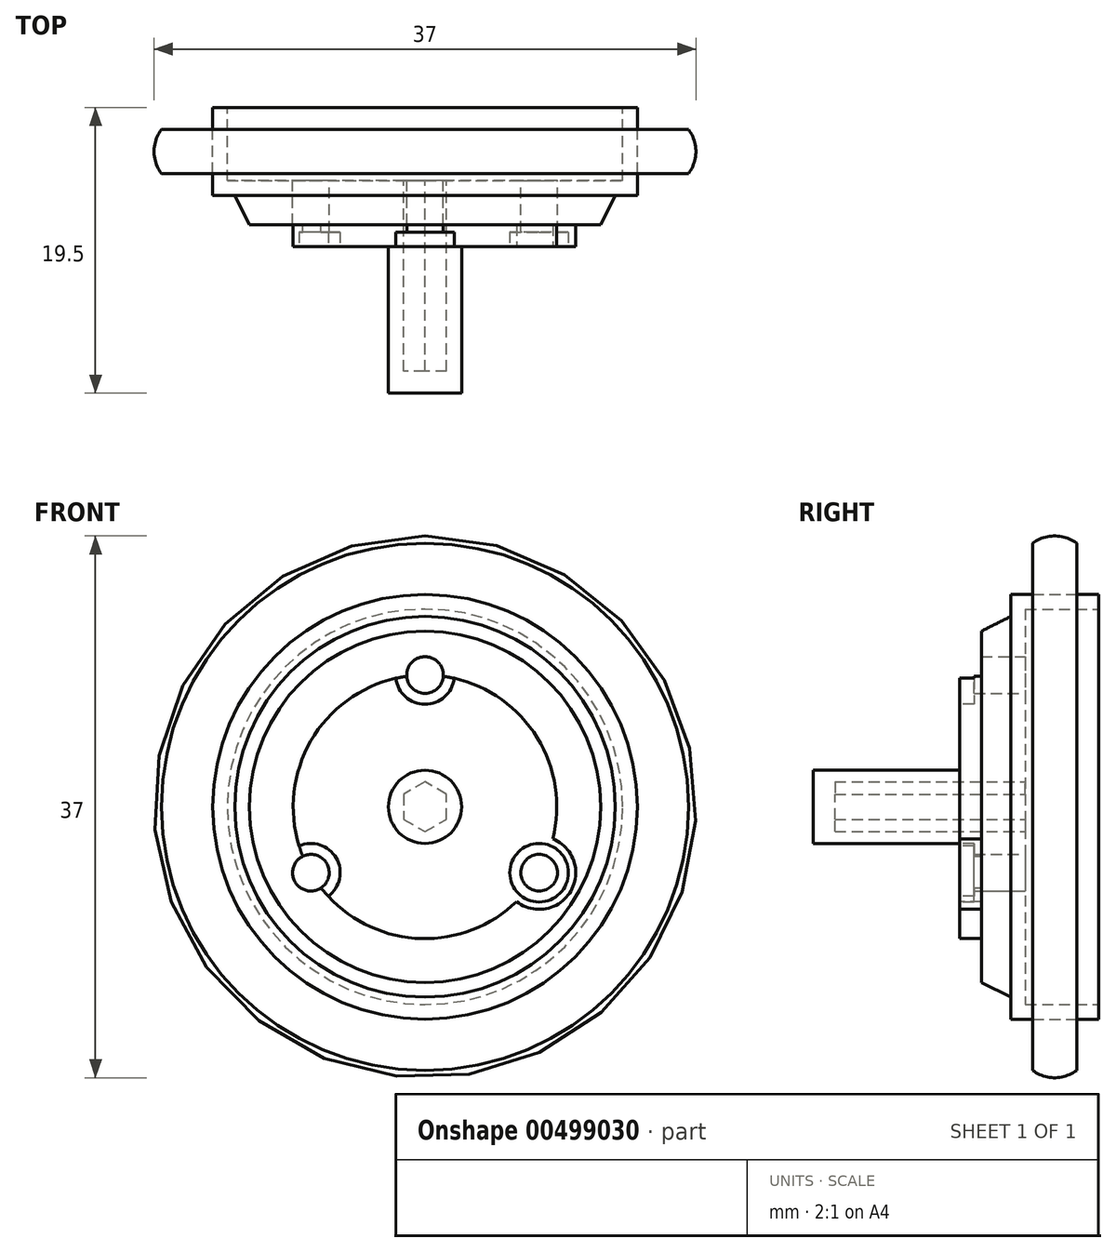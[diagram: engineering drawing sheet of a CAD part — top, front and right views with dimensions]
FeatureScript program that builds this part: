
annotation { "Feature Type Name" : "Feature", "Feature Type Description" : "" }
export const myFeature = defineFeature(function(context is Context, id is Id, definition is map)
    precondition{}
    {
        {
            var Q0;
            Q0=qCreatedBy(makeId("Front.planeOp"),FACE);
            var sketch = newSketch(context, id + "F0", { "sketchPlane" : qUnion([Q0])});
            skCircle(sketch, "E0", {"center": v(0, 0) * mm, "radius": 14.5 * mm});
            skSolve(sketch);
        }
        {
            var Q0;
            Q0=makeQuery(id+"F0.imprint","IMPRINT",FACE,{"disambiguationData":[TD([[makeQuery(id+"F0.imprint","IMPRINT",EDGE,{"derivedFrom":sQuery(id+"F0.wireOp",EDGE,"E0")}),1.0]])]});
            extrude(context, id + "F1", {"entities" : qUnion([Q0]), "depth" : 6 * mm});
        }
        {
            var Q0;
            Q0=qCreatedBy(makeId("Right.planeOp"),FACE);
            var sketch = newSketch(context, id + "F2", { "sketchPlane" : qUnion([Q0])});
            skLineSegment(sketch, "E1.0", {"start": v(-6, -14.5) * mm, "end": v(-6, 14.5) * mm, "construction": true});
            skLineSegment(sketch, "E2", {"start": v(-6, 0) * mm, "end": v(-8, 0) * mm});
            skPoint(sketch, "E2.endSnap0", {"position": v(-6, 0) * mm});
            skLineSegment(sketch, "E3", {"start": v(-8, 0) * mm, "end": v(-8, 12) * mm});
            skLineSegment(sketch, "E4", {"start": v(-8, 12) * mm, "end": v(-6, 13) * mm});
            skLineSegment(sketch, "E5", {"start": v(-6, 13) * mm, "end": v(-6, 0) * mm});
            skSolve(sketch);
        }
        {
            var Q0;
            Q0=makeQuery(id+"F2.imprint","IMPRINT",FACE,{"disambiguationData":[TD([[makeQuery(id+"F2.imprint","IMPRINT",EDGE,{"derivedFrom":sQuery(id+"F2.wireOp",EDGE,"E2")}),-1.0]])]});
            var Q1;
            Q1=sQuery(id+"F2.wireOp",EDGE,"E2");
            revolve(context, id + "F3", {"operationType" : NewBodyOperationType.ADD, "entities" : qUnion([Q0]), "axis" : qUnion([Q1]), "revolveType" : RevolveType.FULL});
        }
        {
            var Q0;
            Q0=makeQuery(id+"F3.opRevolve","SWEPT_FACE",FACE,{"disambiguationData":[OSD([sQuery(id+"F2.wireOp",EDGE,"E3")])]});
            var sketch = newSketch(context, id + "F4", { "sketchPlane" : qUnion([Q0])});
            skCircle(sketch, "E6", {"center": v(0, 0) * mm, "radius": 9 * mm});
            skSolve(sketch);
        }
        {
            var Q0;
            Q0=makeQuery(id+"F4.imprint","IMPRINT",FACE,{"disambiguationData":[TD([[makeQuery(id+"F4.imprint","IMPRINT",EDGE,{"derivedFrom":sQuery(id+"F4.wireOp",EDGE,"E6")}),1.0]])]});
            extrude(context, id + "F5", {"entities" : qUnion([Q0]), "operationType" : NewBodyOperationType.ADD, "depth" : 1.5 * mm});
        }
        {
            var Q0;
            Q0=makeQuery(id+"F5.opExtrude","CAP_FACE",FACE,{"disambiguationData":[OSD([sQuery(id+"F4.wireOp",EDGE,"E6")])],"isStart":false});
            var sketch = newSketch(context, id + "F6", { "sketchPlane" : qUnion([Q0])});
            skCircle(sketch, "E7", {"center": v(0, 0) * mm, "radius": 2.5 * mm});
            skSolve(sketch);
        }
        {
            var Q0;
            Q0=makeQuery(id+"F6.imprint","IMPRINT",FACE,{"disambiguationData":[TD([[makeQuery(id+"F6.imprint","IMPRINT",EDGE,{"derivedFrom":sQuery(id+"F6.wireOp",EDGE,"E7")}),1.0]])]});
            extrude(context, id + "F7", {"entities" : qUnion([Q0]), "operationType" : NewBodyOperationType.ADD, "depth" : 10 * mm});
        }
        {
            var Q0;
            Q0=makeQuery(id+"F5.opExtrude","CAP_FACE",FACE,{"disambiguationData":[OSD([sQuery(id+"F4.wireOp",EDGE,"E6")])],"isStart":false});
            var sketch = newSketch(context, id + "F8", { "sketchPlane" : qUnion([Q0])});
            skCircle(sketch, "E8.0", {"center": v(0, 0) * mm, "radius": 9 * mm, "construction": true});
            skLineSegment(sketch, "E9.0", {"start": v(0, 9) * mm, "end": v(7.8, -4.5) * mm});
            skLineSegment(sketch, "E9.1", {"start": v(7.8, -4.5) * mm, "end": v(-7.8, -4.5) * mm});
            skLineSegment(sketch, "E9.2", {"start": v(-7.8, -4.5) * mm, "end": v(0, 9) * mm});
            skCircle(sketch, "E10", {"center": v(0, 9) * mm, "radius": 2.5 * mm});
            skCircle(sketch, "E11", {"center": v(7.8, -4.5) * mm, "radius": 2.5 * mm});
            skCircle(sketch, "E12", {"center": v(-7.8, -4.5) * mm, "radius": 2.5 * mm});
            skSolve(sketch);
        }
        {
            var Q0;
            {var subQ0=sQuery(id+"F8.wireOp",EDGE,"E9.0");var subQ3=sQuery(id+"F8.wireOp",EDGE,"E11");var subQ4=makeQuery(id+"F8.imprint","INTERSECT",VERTEX,{"derivedFrom":[subQ0,subQ3]});Q0=makeQuery(id+"F8.imprint","IMPRINT",FACE,{"disambiguationData":[TD([[makeQuery(id+"F8.imprint","IMPRINT",EDGE,{"disambiguationData":[TD([[subQ4,1.0]])],"derivedFrom":subQ3}),1.0]])]});}
            var Q1;
            {var subQ0=sQuery(id+"F8.wireOp",EDGE,"E11");var subQ1=makeQuery(id+"F5.opExtrude","CAP_EDGE",EDGE,{"disambiguationData":[OSD([sQuery(id+"F4.wireOp",EDGE,"E6")])],"isStart":false});var subQ2=makeQuery(id+"F8.imprint","INTERSECT",VERTEX,{"disambiguationData":[OD(0.0)],"derivedFrom":[subQ1,subQ0]});Q1=makeQuery(id+"F8.imprint","IMPRINT",FACE,{"disambiguationData":[TD([[makeQuery(id+"F8.imprint","IMPRINT",EDGE,{"disambiguationData":[TD([[subQ2,1.0]])],"derivedFrom":subQ0}),1.0]])]});}
            var Q2;
            {var subQ0=sQuery(id+"F8.wireOp",EDGE,"E9.1");var subQ3=sQuery(id+"F8.wireOp",EDGE,"E11");var subQ4=makeQuery(id+"F8.imprint","INTERSECT",VERTEX,{"derivedFrom":[subQ0,subQ3]});Q2=makeQuery(id+"F8.imprint","IMPRINT",FACE,{"disambiguationData":[TD([[makeQuery(id+"F8.imprint","IMPRINT",EDGE,{"disambiguationData":[TD([[subQ4,-1.0]])],"derivedFrom":subQ3}),1.0]])]});}
            var Q3;
            {var subQ1=sQuery(id+"F8.wireOp",EDGE,"E9.0");var subQ3=sQuery(id+"F8.wireOp",EDGE,"E11");var subQ4=makeQuery(id+"F8.imprint","INTERSECT",VERTEX,{"derivedFrom":[subQ1,subQ3]});Q3=makeQuery(id+"F8.imprint","IMPRINT",FACE,{"disambiguationData":[TD([[makeQuery(id+"F8.imprint","IMPRINT",EDGE,{"disambiguationData":[TD([[subQ4,-1.0]])],"derivedFrom":subQ3}),1.0]])]});}
            var Q4;
            {var subQ1=sQuery(id+"F8.wireOp",EDGE,"E9.1");var subQ3=sQuery(id+"F8.wireOp",EDGE,"E12");var subQ4=makeQuery(id+"F8.imprint","INTERSECT",VERTEX,{"derivedFrom":[subQ1,subQ3]});Q4=makeQuery(id+"F8.imprint","IMPRINT",FACE,{"disambiguationData":[TD([[makeQuery(id+"F8.imprint","IMPRINT",EDGE,{"disambiguationData":[TD([[subQ4,-1.0]])],"derivedFrom":subQ3}),1.0]])]});}
            var Q5;
            {var subQ0=sQuery(id+"F8.wireOp",EDGE,"E9.2");var subQ3=sQuery(id+"F8.wireOp",EDGE,"E12");var subQ4=makeQuery(id+"F8.imprint","INTERSECT",VERTEX,{"derivedFrom":[subQ0,subQ3]});Q5=makeQuery(id+"F8.imprint","IMPRINT",FACE,{"disambiguationData":[TD([[makeQuery(id+"F8.imprint","IMPRINT",EDGE,{"disambiguationData":[TD([[subQ4,-1.0]])],"derivedFrom":subQ3}),1.0]])]});}
            var Q6;
            {var subQ0=sQuery(id+"F8.wireOp",EDGE,"E12");var subQ1=makeQuery(id+"F5.opExtrude","CAP_EDGE",EDGE,{"disambiguationData":[OSD([sQuery(id+"F4.wireOp",EDGE,"E6")])],"isStart":false});var subQ2=makeQuery(id+"F8.imprint","INTERSECT",VERTEX,{"disambiguationData":[OD(0.0)],"derivedFrom":[subQ1,subQ0]});Q6=makeQuery(id+"F8.imprint","IMPRINT",FACE,{"disambiguationData":[TD([[makeQuery(id+"F8.imprint","IMPRINT",EDGE,{"disambiguationData":[TD([[subQ2,-1.0]])],"derivedFrom":subQ0}),1.0]])]});}
            var Q7;
            {var subQ0=sQuery(id+"F8.wireOp",EDGE,"E9.1");var subQ3=sQuery(id+"F8.wireOp",EDGE,"E12");var subQ4=makeQuery(id+"F8.imprint","INTERSECT",VERTEX,{"derivedFrom":[subQ0,subQ3]});Q7=makeQuery(id+"F8.imprint","IMPRINT",FACE,{"disambiguationData":[TD([[makeQuery(id+"F8.imprint","IMPRINT",EDGE,{"disambiguationData":[TD([[subQ4,1.0]])],"derivedFrom":subQ3}),1.0]])]});}
            var Q8;
            {var subQ0=sQuery(id+"F8.wireOp",EDGE,"E9.2");var subQ3=sQuery(id+"F8.wireOp",EDGE,"E10");var subQ4=makeQuery(id+"F8.imprint","INTERSECT",VERTEX,{"derivedFrom":[subQ0,subQ3]});Q8=makeQuery(id+"F8.imprint","IMPRINT",FACE,{"disambiguationData":[TD([[makeQuery(id+"F8.imprint","IMPRINT",EDGE,{"disambiguationData":[TD([[subQ4,1.0]])],"derivedFrom":subQ3}),1.0]])]});}
            var Q9;
            {var subQ1=sQuery(id+"F8.wireOp",EDGE,"E9.0");var subQ3=sQuery(id+"F8.wireOp",EDGE,"E10");var subQ4=makeQuery(id+"F8.imprint","INTERSECT",VERTEX,{"derivedFrom":[subQ1,subQ3]});Q9=makeQuery(id+"F8.imprint","IMPRINT",FACE,{"disambiguationData":[TD([[makeQuery(id+"F8.imprint","IMPRINT",EDGE,{"disambiguationData":[TD([[subQ4,1.0]])],"derivedFrom":subQ3}),1.0]])]});}
            var Q10;
            {var subQ0=sQuery(id+"F8.wireOp",EDGE,"E9.0");var subQ3=sQuery(id+"F8.wireOp",EDGE,"E10");var subQ4=makeQuery(id+"F8.imprint","INTERSECT",VERTEX,{"derivedFrom":[subQ0,subQ3]});Q10=makeQuery(id+"F8.imprint","IMPRINT",FACE,{"disambiguationData":[TD([[makeQuery(id+"F8.imprint","IMPRINT",EDGE,{"disambiguationData":[TD([[subQ4,-1.0]])],"derivedFrom":subQ3}),1.0]])]});}
            var Q11;
            {var subQ0=sQuery(id+"F8.wireOp",EDGE,"E10");var subQ1=makeQuery(id+"F5.opExtrude","CAP_EDGE",EDGE,{"disambiguationData":[OSD([sQuery(id+"F4.wireOp",EDGE,"E6")])],"isStart":false});var subQ2=makeQuery(id+"F8.imprint","INTERSECT",VERTEX,{"disambiguationData":[OD(0.0)],"derivedFrom":[subQ1,subQ0]});Q11=makeQuery(id+"F8.imprint","IMPRINT",FACE,{"disambiguationData":[TD([[makeQuery(id+"F8.imprint","IMPRINT",EDGE,{"disambiguationData":[TD([[subQ2,1.0]])],"derivedFrom":subQ0}),1.0]])]});}
            extrude(context, id + "F9", {"entities" : qUnion([Q0, Q1, Q2, Q3, Q4, Q5, Q6, Q7, Q8, Q9, Q10, Q11]), "operationType" : NewBodyOperationType.ADD, "oppositeDirection" : true, "depth" : 9 * mm});
        }
        {
            var Q0;
            Q0=makeQuery(id+"F1.opExtrude","CAP_FACE",FACE,{"disambiguationData":[OSD([sQuery(id+"F0.wireOp",EDGE,"E0")])],"isStart":true});
            var sketch = newSketch(context, id + "F10", { "sketchPlane" : qUnion([Q0])});
            skCircle(sketch, "E13", {"center": v(0, 0) * mm, "radius": 13.5 * mm});
            skSolve(sketch);
        }
        {
            var Q0;
            Q0=makeQuery(id+"F10.imprint","IMPRINT",FACE,{"disambiguationData":[TD([[makeQuery(id+"F10.imprint","IMPRINT",EDGE,{"derivedFrom":sQuery(id+"F10.wireOp",EDGE,"E13")}),1.0]])]});
            extrude(context, id + "F11", {"entities" : qUnion([Q0]), "operationType" : NewBodyOperationType.REMOVE, "oppositeDirection" : true, "depth" : 5 * mm});
        }
        {
            var Q0;
            Q0=makeQuery(id+"F11.boolean.opBoolean","COPY",FACE,{"derivedFrom":makeQuery(id+"F11.opExtrude","CAP_FACE",FACE,{"disambiguationData":[OSD([sQuery(id+"F10.wireOp",EDGE,"E13")])],"isStart":false})});
            var sketch = newSketch(context, id + "F12", { "sketchPlane" : qUnion([Q0])});
            skCircle(sketch, "E14.cCircle", {"center": v(0, 0) * mm, "radius": 1.7 * mm, "construction": true});
            skLineSegment(sketch, "E14.0", {"start": v(0, 1.7) * mm, "end": v(1.47, 0.85) * mm});
            skLineSegment(sketch, "E14.1", {"start": v(1.47, 0.85) * mm, "end": v(1.47, -0.85) * mm});
            skLineSegment(sketch, "E14.2", {"start": v(1.47, -0.85) * mm, "end": v(0, -1.7) * mm});
            skLineSegment(sketch, "E14.3", {"start": v(0, -1.7) * mm, "end": v(-1.47, -0.85) * mm});
            skLineSegment(sketch, "E14.4", {"start": v(-1.47, -0.85) * mm, "end": v(-1.47, 0.85) * mm});
            skLineSegment(sketch, "E14.5", {"start": v(-1.47, 0.85) * mm, "end": v(0, 1.7) * mm});
            skSolve(sketch);
        }
        {
            var Q0;
            Q0=makeQuery(id+"F12.imprint","IMPRINT",FACE,{"disambiguationData":[TD([[makeQuery(id+"F12.imprint","IMPRINT",EDGE,{"derivedFrom":sQuery(id+"F12.wireOp",EDGE,"E14.0")}),-1.0]])]});
            extrude(context, id + "F13", {"entities" : qUnion([Q0]), "operationType" : NewBodyOperationType.REMOVE, "oppositeDirection" : true, "offsetDistance" : 25 * mm, "depth" : 13 * mm});
        }
        {
            var Q0;
            Q0=qCreatedBy(makeId("Top.planeOp"),FACE);
            var sketch = newSketch(context, id + "F14", { "sketchPlane" : qUnion([Q0])});
            skLineSegment(sketch, "E15", {"start": v(14.5, 0) * mm, "end": v(14.5, -6) * mm, "construction": true});
            skLineSegment(sketch, "E16", {"start": v(14.5, -3) * mm, "end": v(14.5, -1.5) * mm});
            skLineSegment(sketch, "E17", {"start": v(14.5, -3) * mm, "end": v(14.5, -4.5) * mm});
            skLineSegment(sketch, "E18", {"start": v(14.5, -1.5) * mm, "end": v(18, -1.5) * mm});
            skLineSegment(sketch, "E19", {"start": v(14.5, -4.5) * mm, "end": v(18, -4.5) * mm});
            skArc(sketch, "E20", {"start": v(18, -4.5) * mm, "mid": v(18.5, -3) * mm, "end": v(18, -1.5) * mm});
            skLineSegment(sketch, "E21.0", {"start": v(14.5, 0) * mm, "end": v(-14.5, 0) * mm, "construction": true});
            skLineSegment(sketch, "E22.0", {"start": v(14.5, -6) * mm, "end": v(-14.5, -6) * mm, "construction": true});
            skLineSegment(sketch, "E23", {"start": v(0, 0) * mm, "end": v(0, -6) * mm, "construction": true});
            skSolve(sketch);
        }
        {
            var Q0;
            Q0=makeQuery(id+"F14.imprint","IMPRINT",FACE,{"disambiguationData":[TD([[makeQuery(id+"F14.imprint","IMPRINT",EDGE,{"derivedFrom":sQuery(id+"F14.wireOp",EDGE,"E16")}),-1.0]])]});
            var Q1;
            Q1=sQuery(id+"F14.wireOp",EDGE,"E23");
            revolve(context, id + "F15", {"entities" : qUnion([Q0]), "axis" : qUnion([Q1]), "revolveType" : RevolveType.FULL});
        }
        {
            var Q0;
            Q0=makeQuery(id+"F9.boolean.opBoolean","MERGE",FACE,{"derivedFrom":[makeQuery(id+"F5.opExtrude","CAP_FACE",FACE,{"disambiguationData":[OSD([sQuery(id+"F4.wireOp",EDGE,"E6")])],"isStart":false}),makeQuery(id+"F9.opExtrude","CAP_FACE",FACE,{"disambiguationData":[OSD([sQuery(id+"F8.wireOp",EDGE,"E10")])],"isStart":true}),makeQuery(id+"F9.opExtrude","CAP_FACE",FACE,{"disambiguationData":[OSD([sQuery(id+"F8.wireOp",EDGE,"E11")])],"isStart":true}),makeQuery(id+"F9.opExtrude","CAP_FACE",FACE,{"disambiguationData":[OSD([sQuery(id+"F8.wireOp",EDGE,"E12")])],"isStart":true})]});
            var sketch = newSketch(context, id + "F16", { "sketchPlane" : qUnion([Q0])});
            skCircle(sketch, "E24", {"center": v(0, 9) * mm, "radius": 2 * mm});
            skCircle(sketch, "E25", {"center": v(7.8, -4.5) * mm, "radius": 2 * mm});
            skCircle(sketch, "E26", {"center": v(-7.8, -4.5) * mm, "radius": 2 * mm});
            skSolve(sketch);
        }
        {
            var Q0;
            Q0=makeQuery(id+"F11.boolean.opBoolean","COPY",FACE,{"derivedFrom":makeQuery(id+"F11.opExtrude","CAP_FACE",FACE,{"disambiguationData":[OSD([sQuery(id+"F10.wireOp",EDGE,"E13")])],"isStart":false})});
            var sketch = newSketch(context, id + "F17", { "sketchPlane" : qUnion([Q0])});
            skSolve(sketch);
        }
        {
            var Q0;
            Q0=makeQuery(id+"F17.imprint","IMPRINT",FACE,{"disambiguationData":[TD([[makeQuery(id+"F17.imprint","IMPRINT",EDGE,{"derivedFrom":makeQuery(id+"F11.boolean.opBoolean","COPY",EDGE,{"derivedFrom":makeQuery(id+"F11.opExtrude","CAP_EDGE",EDGE,{"disambiguationData":[OSD([sQuery(id+"F10.wireOp",EDGE,"E13")])],"isStart":false})})}),1.0]])]});
            var sketch = newSketch(context, id + "F18", { "sketchPlane" : qUnion([Q0])});
            skPoint(sketch, "E27.0", {"position": v(-7.8, -4.5) * mm});
            skPoint(sketch, "E27.1", {"position": v(7.8, -4.5) * mm});
            skPoint(sketch, "E27.2", {"position": v(0, 9) * mm});
            skCircle(sketch, "E28", {"center": v(-7.8, -4.5) * mm, "radius": 1.25 * mm});
            skCircle(sketch, "E29", {"center": v(7.8, -4.5) * mm, "radius": 1.25 * mm});
            skCircle(sketch, "E30", {"center": v(0, 9) * mm, "radius": 1.25 * mm});
            skSolve(sketch);
        }
        {
            var Q0;
            Q0=makeQuery(id+"F18.imprint","IMPRINT",FACE,{"disambiguationData":[TD([[makeQuery(id+"F18.imprint","IMPRINT",EDGE,{"derivedFrom":sQuery(id+"F18.wireOp",EDGE,"E29")}),1.0]])]});
            var Q1;
            Q1=makeQuery(id+"F18.imprint","IMPRINT",FACE,{"disambiguationData":[TD([[makeQuery(id+"F18.imprint","IMPRINT",EDGE,{"derivedFrom":sQuery(id+"F18.wireOp",EDGE,"E30")}),1.0]])]});
            var Q2;
            Q2=makeQuery(id+"F18.imprint","IMPRINT",FACE,{"disambiguationData":[TD([[makeQuery(id+"F18.imprint","IMPRINT",EDGE,{"derivedFrom":sQuery(id+"F18.wireOp",EDGE,"E28")}),1.0]])]});
            var Q3;
            Q3=sQuery(id+"F18.wireOp",EDGE,"E28");
            extrude(context, id + "F19", {"entities" : qUnion([Q0, Q1, Q2]), "operationType" : NewBodyOperationType.REMOVE, "surfaceEntities" : qUnion([Q3]), "oppositeDirection" : true, "depth" : 4.5 * mm});
        }
        {
            var Q0;
            Q0=makeQuery(id+"F16.imprint","IMPRINT",FACE,{"disambiguationData":[TD([[makeQuery(id+"F16.imprint","IMPRINT",EDGE,{"derivedFrom":sQuery(id+"F16.wireOp",EDGE,"E26")}),1.0]])]});
            var Q1;
            Q1=makeQuery(id+"F16.imprint","IMPRINT",FACE,{"disambiguationData":[TD([[makeQuery(id+"F16.imprint","IMPRINT",EDGE,{"derivedFrom":sQuery(id+"F16.wireOp",EDGE,"E25")}),1.0]])]});
            var Q2;
            Q2=makeQuery(id+"F16.imprint","IMPRINT",FACE,{"disambiguationData":[TD([[makeQuery(id+"F16.imprint","IMPRINT",EDGE,{"derivedFrom":sQuery(id+"F16.wireOp",EDGE,"E24")}),1.0]])]});
            extrude(context, id + "F20", {"entities" : qUnion([Q0, Q1, Q2]), "operationType" : NewBodyOperationType.REMOVE, "oppositeDirection" : true, "depth" : 1 * mm});
        }
    });
